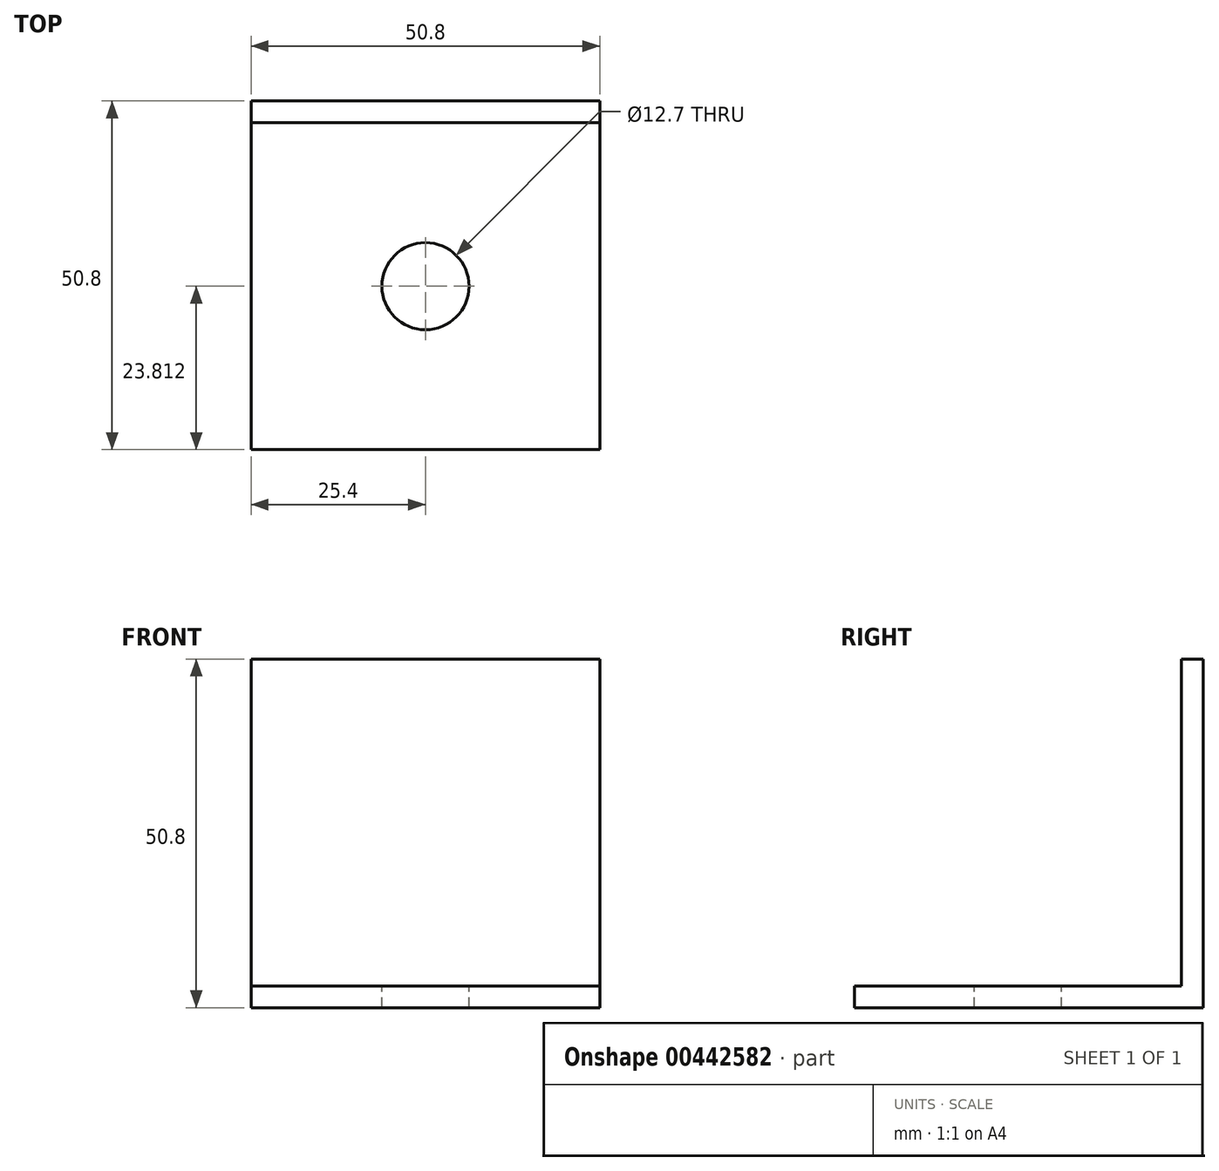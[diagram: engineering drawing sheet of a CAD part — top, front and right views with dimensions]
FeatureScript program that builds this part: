
annotation { "Feature Type Name" : "Feature", "Feature Type Description" : "" }
export const myFeature = defineFeature(function(context is Context, id is Id, definition is map)
    precondition{}
    {
        {
            var Q0;
            Q0=qCreatedBy(makeId("Right.planeOp"),FACE);
            var sketch = newSketch(context, id + "F0", { "sketchPlane" : qUnion([Q0])});
            skLineSegment(sketch, "E0.bottom", {"start": v(0, 0) * mm, "end": v(-50.8, 0) * mm});
            skLineSegment(sketch, "E0.top", {"start": v(0, 50.8) * mm, "end": v(-3.18, 50.8) * mm});
            skLineSegment(sketch, "E0.left", {"start": v(0, 0) * mm, "end": v(0, 50.8) * mm});
            skLineSegment(sketch, "E0.right", {"start": v(-50.8, 0) * mm, "end": v(-50.8, 3.17) * mm});
            skLineSegment(sketch, "E1.top", {"start": v(-50.8, 3.17) * mm, "end": v(-3.17, 3.17) * mm});
            skLineSegment(sketch, "E1.right", {"start": v(-3.18, 50.8) * mm, "end": v(-3.17, 3.17) * mm});
            skSolve(sketch);
        }
        {
            var Q0;
            Q0 = qSketchRegion(id + "F0", true);
            extrude(context, id + "F1", {"entities" : qUnion([Q0]), "depth" : 50.8 * mm});
        }
        {
            var Q0;
            Q0=makeQuery(id+"F1.opExtrude","SWEPT_FACE",FACE,{"disambiguationData":[OSD([sQuery(id+"F0.wireOp",EDGE,"E1.top")])]});
            var sketch = newSketch(context, id + "F2", { "sketchPlane" : qUnion([Q0])});
            skCircle(sketch, "E2", {"center": v(25.4, -26.99) * mm, "radius": 6.35 * mm});
            skSolve(sketch);
        }
        {
            var Q0;
            Q0 = qSketchRegion(id + "F2", true);
            extrude(context, id + "F3", {"entities" : qUnion([Q0]), "operationType" : NewBodyOperationType.REMOVE, "oppositeDirection" : true, "depth" : 25.4 * mm});
        }
    });
